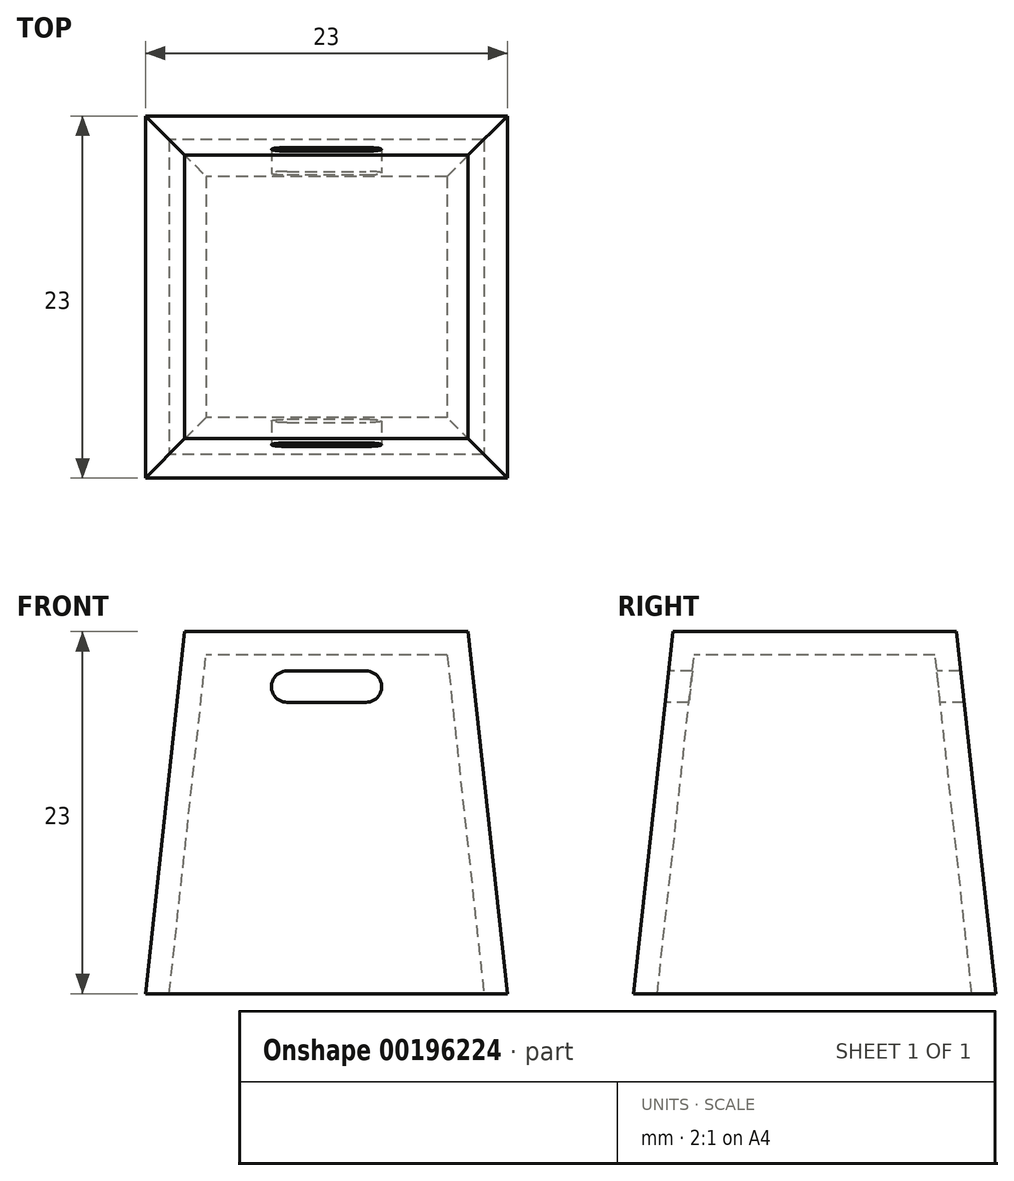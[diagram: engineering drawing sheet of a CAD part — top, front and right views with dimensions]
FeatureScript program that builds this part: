
annotation { "Feature Type Name" : "Feature", "Feature Type Description" : "" }
export const myFeature = defineFeature(function(context is Context, id is Id, definition is map)
    precondition{}
    {
        {
            var Q0;
            Q0=qCreatedBy(makeId("Top.planeOp"),FACE);
            cPlane(context, id + "F0", {"entities" : qUnion([Q0]), "cplaneType" : CPlaneType.OFFSET, "offset" : (460 / 20) * mm, "width" : 150 * mm, "height" : 150 * mm});
        }
        {
            var Q0;
            Q0=qCreatedBy(makeId("Top.planeOp"),FACE);
            var sketch = newSketch(context, id + "F1", { "sketchPlane" : qUnion([Q0])});
            skLineSegment(sketch, "E0.bottom", {"start": v(11.5, 11.5) * mm, "end": v(-11.5, 11.5) * mm});
            skLineSegment(sketch, "E0.top", {"start": v(11.5, -11.5) * mm, "end": v(-11.5, -11.5) * mm});
            skLineSegment(sketch, "E0.left", {"start": v(11.5, 11.5) * mm, "end": v(11.5, -11.5) * mm});
            skLineSegment(sketch, "E0.right", {"start": v(-11.5, 11.5) * mm, "end": v(-11.5, -11.5) * mm});
            skPoint(sketch, "E0.middle", {"position": v(0, 0) * mm});
            skSolve(sketch);
        }
        {
            var Q0;
            Q0=qCreatedBy(id+"F0.planeOp",FACE);
            var sketch = newSketch(context, id + "F2", { "sketchPlane" : qUnion([Q0])});
            skLineSegment(sketch, "E1.bottom", {"start": v(9, 9) * mm, "end": v(-9, 9) * mm});
            skLineSegment(sketch, "E1.top", {"start": v(9, -9) * mm, "end": v(-9, -9) * mm});
            skLineSegment(sketch, "E1.left", {"start": v(9, 9) * mm, "end": v(9, -9) * mm});
            skLineSegment(sketch, "E1.right", {"start": v(-9, 9) * mm, "end": v(-9, -9) * mm});
            skPoint(sketch, "E1.middle", {"position": v(0, 0) * mm});
            skSolve(sketch);
        }
        {
            var Q0;
            Q0=makeQuery(id+"F1.imprint","IMPRINT",FACE,{"disambiguationData":[TD([[makeQuery(id+"F1.imprint","IMPRINT",EDGE,{"derivedFrom":sQuery(id+"F1.wireOp",EDGE,"E0.bottom")}),1.0]])]});
            var Q1;
            Q1=makeQuery(id+"F2.imprint","IMPRINT",FACE,{"disambiguationData":[TD([[makeQuery(id+"F2.imprint","IMPRINT",EDGE,{"derivedFrom":sQuery(id+"F2.wireOp",EDGE,"E1.bottom")}),1.0]])]});
            loft(context, id + "F3", {"sheetProfilesArray" : [{ "sheetProfileEntities" : qUnion([Q0]) }, { "sheetProfileEntities" : qUnion([Q1]) }]});
        }
        {
            var Q0;
            Q0=makeQuery(id+"F3.opLoft","CAP_FACE",FACE,{"disambiguationData":[OSD([makeQuery(id+"F1.imprint","IMPRINT",FACE,{"disambiguationData":[TD([[makeQuery(id+"F1.imprint","IMPRINT",EDGE,{"derivedFrom":sQuery(id+"F1.wireOp",EDGE,"E0.bottom")}),1.0]])]})])],"isStart":true});
            shell(context, id + "F4", {"entities" : qUnion([Q0]), "thickness" : 1.5 * mm});
        }
        {
            var Q0;
            Q0=qCreatedBy(makeId("Front.planeOp"),FACE);
            var sketch = newSketch(context, id + "F5", { "sketchPlane" : qUnion([Q0])});
            skLineSegment(sketch, "E2.bottom", {"start": v(3.5, 18.5) * mm, "end": v(-3.5, 18.5) * mm});
            skLineSegment(sketch, "E2.top", {"start": v(3.5, 20.5) * mm, "end": v(-3.5, 20.5) * mm});
            skLineSegment(sketch, "E2.left", {"start": v(3.5, 18.5) * mm, "end": v(3.5, 20.5) * mm});
            skLineSegment(sketch, "E2.right", {"start": v(-3.5, 18.5) * mm, "end": v(-3.5, 20.5) * mm});
            skPoint(sketch, "E2.middle", {"position": v(0, 19.5) * mm});
            skSolve(sketch);
        }
        {
            var Q0;
            Q0=makeQuery(id+"F5.imprint","IMPRINT",FACE,{"disambiguationData":[TD([[makeQuery(id+"F5.imprint","IMPRINT",EDGE,{"derivedFrom":sQuery(id+"F5.wireOp",EDGE,"E2.bottom")}),-1.0]])]});
            extrude(context, id + "F6", {"entities" : qUnion([Q0]), "operationType" : NewBodyOperationType.REMOVE, "endBound" : BoundingType.THROUGH_ALL, "oppositeDirection" : true, "depth" : 5 * mm, "hasSecondDirection" : true, "secondDirectionBound" : SecondDirectionBoundingType.THROUGH_ALL, "secondDirectionOppositeDirection" : false, "secondDirectionDepth" : 25 * mm});
        }
        {
            var Q0;
            Q0=makeQuery(id+"F6.boolean.opBoolean","COPY",EDGE,{"derivedFrom":makeQuery(id+"F6.opExtrude","SWEPT_EDGE",EDGE,{"disambiguationData":[OSD([sQuery(id+"F5.wireOp",EDGE,"E2.top"),sQuery(id+"F5.wireOp",EDGE,"E2.right")])]})});
            var Q1;
            Q1=makeQuery(id+"F6.boolean.opBoolean","COPY",EDGE,{"derivedFrom":makeQuery(id+"F6.opExtrude","SWEPT_EDGE",EDGE,{"disambiguationData":[OSD([sQuery(id+"F5.wireOp",EDGE,"E2.bottom"),sQuery(id+"F5.wireOp",EDGE,"E2.right")])]})});
            var Q2;
            Q2=makeQuery(id+"F6.boolean.opBoolean","COPY",EDGE,{"derivedFrom":makeQuery(id+"F6.opExtrude","SWEPT_EDGE",EDGE,{"disambiguationData":[OSD([sQuery(id+"F5.wireOp",EDGE,"E2.bottom"),sQuery(id+"F5.wireOp",EDGE,"E2.left")])]})});
            var Q3;
            Q3=makeQuery(id+"F6.boolean.opBoolean","COPY",EDGE,{"derivedFrom":makeQuery(id+"F6.opExtrude","SWEPT_EDGE",EDGE,{"disambiguationData":[OSD([sQuery(id+"F5.wireOp",EDGE,"E2.top"),sQuery(id+"F5.wireOp",EDGE,"E2.left")])]})});
            fillet(context, id + "F7", {"entities" : qUnion([Q0, Q1, Q2, Q3]), "radius" : 1 * mm, "tangentPropagation" : true, "allowEdgeOverflow" : false});
        }
    });
